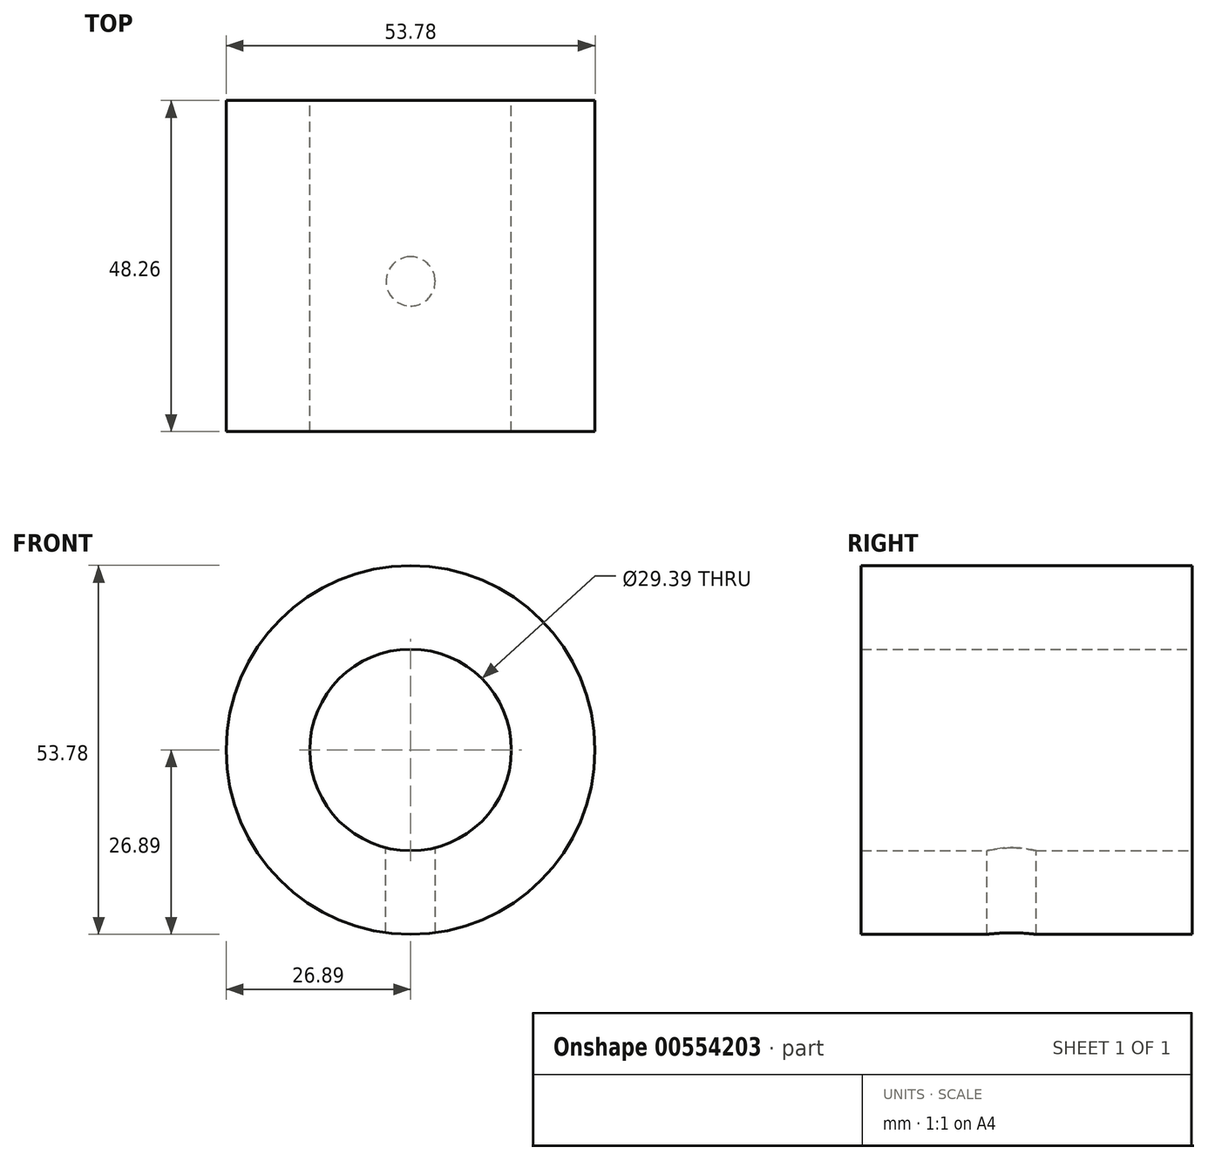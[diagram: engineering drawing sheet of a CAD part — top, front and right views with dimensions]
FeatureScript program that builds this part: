
annotation { "Feature Type Name" : "Feature", "Feature Type Description" : "" }
export const myFeature = defineFeature(function(context is Context, id is Id, definition is map)
    precondition{}
    {
        {
            var Q0;
            Q0=qCreatedBy(makeId("Front.planeOp"),FACE);
            var sketch = newSketch(context, id + "F0", { "sketchPlane" : qUnion([Q0])});
            skCircle(sketch, "E0", {"center": v(0, 0) * mm, "radius": 26.89 * mm});
            skCircle(sketch, "E1", {"center": v(0, 0) * mm, "radius": 14.7 * mm});
            skSolve(sketch);
        }
        {
            var Q0;
            Q0=makeQuery(id+"F0.imprint","IMPRINT",FACE,{"disambiguationData":[TD([[makeQuery(id+"F0.imprint","IMPRINT",EDGE,{"derivedFrom":sQuery(id+"F0.wireOp",EDGE,"E0")}),1.0]])]});
            extrude(context, id + "F1", {"entities" : qUnion([Q0]), "depth" : 48.26 * mm, "offsetDistance" : 25.4 * mm});
        }
        {
            var Q0;
            Q0=qCreatedBy(makeId("Top.planeOp"),FACE);
            var sketch = newSketch(context, id + "F2", { "sketchPlane" : qUnion([Q0])});
            skCircle(sketch, "E2", {"center": v(0, -26.36) * mm, "radius": 3.6 * mm});
            skSolve(sketch);
        }
        {
            var Q0;
            Q0=makeQuery(id+"F2.imprint","IMPRINT",FACE,{"disambiguationData":[TD([[makeQuery(id+"F2.imprint","IMPRINT",EDGE,{"derivedFrom":sQuery(id+"F2.wireOp",EDGE,"E2")}),1.0]])]});
            extrude(context, id + "F3", {"entities" : qUnion([Q0]), "operationType" : NewBodyOperationType.REMOVE, "oppositeDirection" : true, "depth" : 42.67 * mm, "offsetDistance" : 25.4 * mm});
        }
    });
